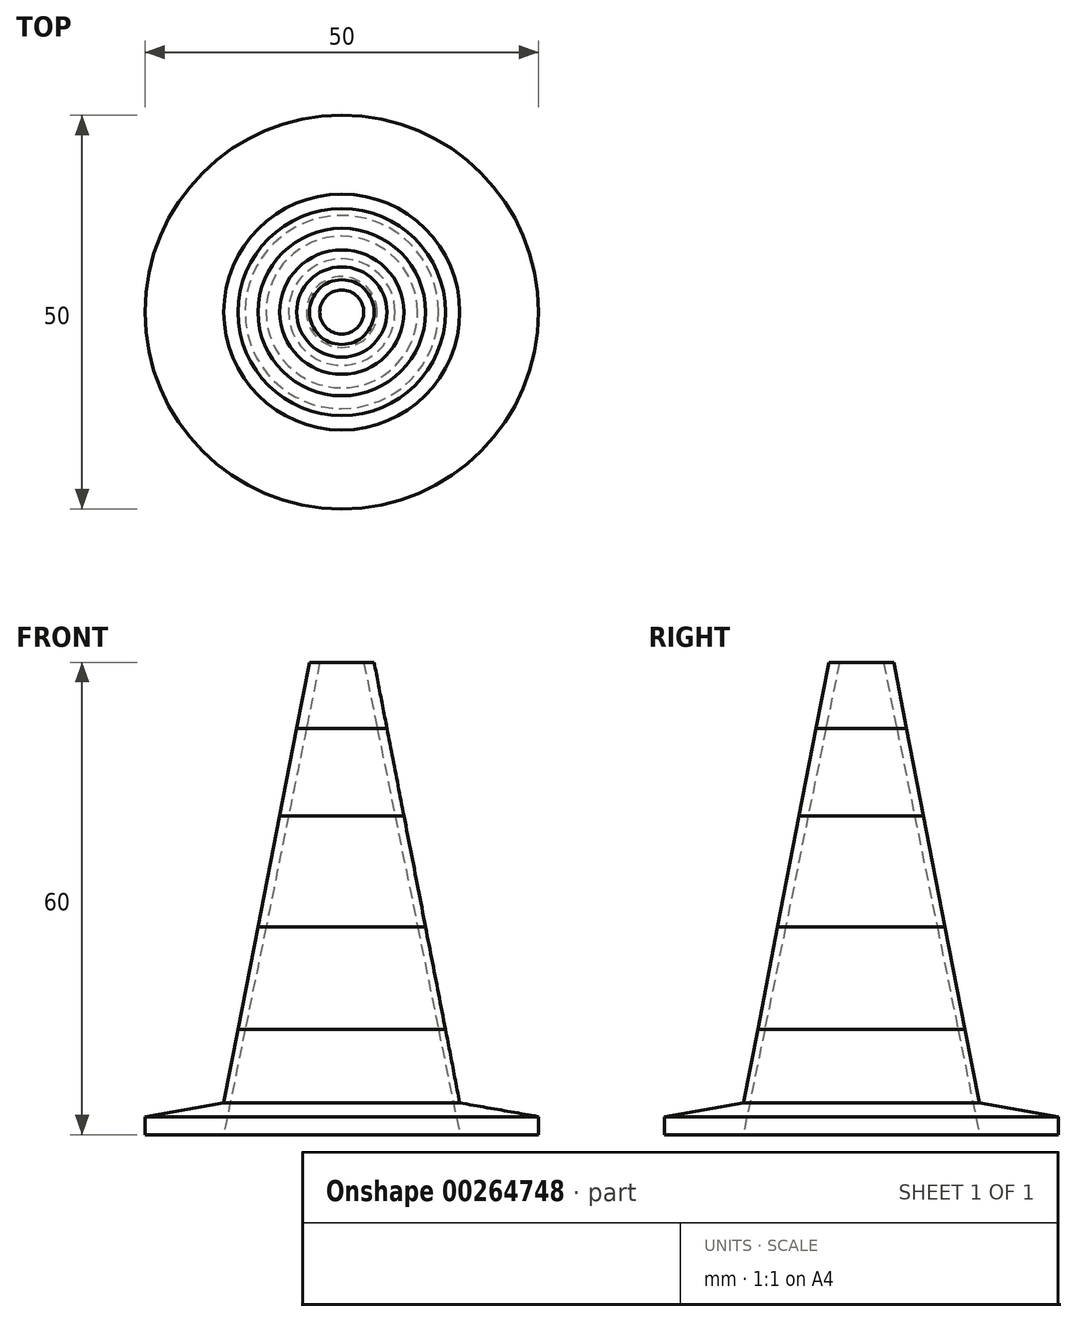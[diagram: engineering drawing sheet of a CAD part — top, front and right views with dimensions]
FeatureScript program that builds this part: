
annotation { "Feature Type Name" : "Feature", "Feature Type Description" : "" }
export const myFeature = defineFeature(function(context is Context, id is Id, definition is map)
    precondition{}
    {
        {
            var Q0;
            Q0=qCreatedBy(makeId("Front.planeOp"),FACE);
            var sketch = newSketch(context, id + "F0", { "sketchPlane" : qUnion([Q0])});
            skLineSegment(sketch, "E0", {"start": v(-25, 0) * mm, "end": v(-25, 2.28) * mm});
            skLineSegment(sketch, "E1", {"start": v(-25, 2.28) * mm, "end": v(-14.98, 4.05) * mm});
            skLineSegment(sketch, "E2", {"start": v(-14.98, 4.05) * mm, "end": v(-4.1, 60) * mm});
            skLineSegment(sketch, "E3", {"start": v(-4.1, 60) * mm, "end": v(0, 60) * mm});
            skLineSegment(sketch, "E4", {"start": v(0, 60) * mm, "end": v(0, 0) * mm});
            skLineSegment(sketch, "E5", {"start": v(0, 0) * mm, "end": v(-25, 0) * mm});
            skLineSegment(sketch, "E6", {"start": v(-13.17, 13.4) * mm, "end": v(0, 13.4) * mm});
            skLineSegment(sketch, "E7", {"start": v(-10.64, 26.4) * mm, "end": v(0, 26.4) * mm});
            skLineSegment(sketch, "E8", {"start": v(-7.9, 40.5) * mm, "end": v(0, 40.5) * mm});
            skPoint(sketch, "E8.endSnap0", {"position": v(0, 30) * mm});
            skLineSegment(sketch, "E9", {"start": v(-5.74, 51.6) * mm, "end": v(0, 51.6) * mm});
            skSolve(sketch);
        }
        {
            var Q0;
            {var subQ0=sQuery(id+"F0.wireOp",EDGE,"E3");Q0=makeQuery(id+"F0.imprint","IMPRINT",FACE,{"disambiguationData":[TD([[makeQuery(id+"F0.imprint","IMPRINT",EDGE,{"derivedFrom":subQ0}),-1.0]])]});}
            var Q1;
            Q1=sQuery(id+"F0.wireOp",EDGE,"E4");
            revolve(context, id + "F1", {"entities" : qUnion([Q0]), "axis" : qUnion([Q1]), "revolveType" : RevolveType.FULL});
        }
        {
            var Q0;
            {var subQ0=sQuery(id+"F0.wireOp",EDGE,"E8");Q0=makeQuery(id+"F0.imprint","IMPRINT",FACE,{"disambiguationData":[TD([[makeQuery(id+"F0.imprint","IMPRINT",EDGE,{"derivedFrom":subQ0}),1.0]])]});}
            var Q1;
            Q1=sQuery(id+"F0.wireOp",EDGE,"E4");
            revolve(context, id + "F2", {"entities" : qUnion([Q0]), "axis" : qUnion([Q1]), "revolveType" : RevolveType.FULL});
        }
        {
            var Q0;
            {var subQ0=sQuery(id+"F0.wireOp",EDGE,"E7");Q0=makeQuery(id+"F0.imprint","IMPRINT",FACE,{"disambiguationData":[TD([[makeQuery(id+"F0.imprint","IMPRINT",EDGE,{"derivedFrom":subQ0}),1.0]])]});}
            var Q1;
            Q1=sQuery(id+"F0.wireOp",EDGE,"E4");
            revolve(context, id + "F3", {"entities" : qUnion([Q0]), "axis" : qUnion([Q1]), "revolveType" : RevolveType.FULL});
        }
        {
            var Q0;
            {var subQ0=sQuery(id+"F0.wireOp",EDGE,"E6");Q0=makeQuery(id+"F0.imprint","IMPRINT",FACE,{"disambiguationData":[TD([[makeQuery(id+"F0.imprint","IMPRINT",EDGE,{"derivedFrom":subQ0}),1.0]])]});}
            var Q1;
            Q1=sQuery(id+"F0.wireOp",EDGE,"E4");
            revolve(context, id + "F4", {"entities" : qUnion([Q0]), "axis" : qUnion([Q1]), "revolveType" : RevolveType.FULL});
        }
        {
            var Q0;
            Q0=makeQuery(id+"F0.imprint","IMPRINT",FACE,{"disambiguationData":[TD([[makeQuery(id+"F0.imprint","IMPRINT",EDGE,{"derivedFrom":sQuery(id+"F0.wireOp",EDGE,"E0")}),-1.0]])]});
            var Q1;
            Q1=sQuery(id+"F0.wireOp",EDGE,"E4");
            revolve(context, id + "F5", {"entities" : qUnion([Q0]), "axis" : qUnion([Q1]), "revolveType" : RevolveType.FULL});
        }
        {
            var Q0;
            Q0=makeQuery(id+"F5.opRevolve","SWEPT_FACE",FACE,{"disambiguationData":[OSD([sQuery(id+"F0.wireOp",EDGE,"E5")])]});
            var sketch = newSketch(context, id + "F6", { "sketchPlane" : qUnion([Q0])});
            skCircle(sketch, "E10", {"center": v(0, 0) * mm, "radius": 15 * mm});
            skSolve(sketch);
        }
        {
            var Q0;
            Q0 = qSketchRegion(id + "F6", true);
            extrude(context, id + "F7", {"entities" : qUnion([Q0]), "operationType" : NewBodyOperationType.REMOVE, "oppositeDirection" : true, "depth" : 62.23 * mm, "hasDraft" : true, "draftAngle" : 11.5 * degree, "draftPullDirection" : true});
        }
    });
